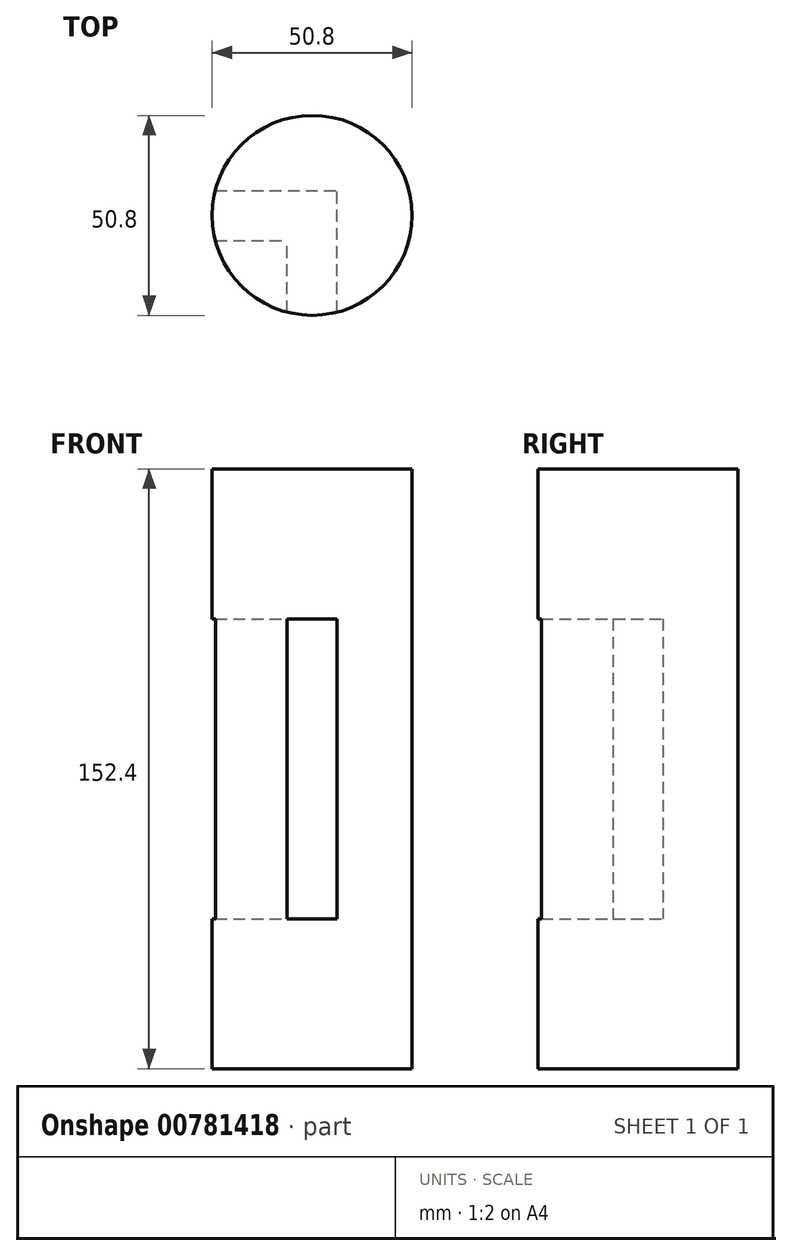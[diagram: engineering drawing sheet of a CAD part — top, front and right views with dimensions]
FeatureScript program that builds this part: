
annotation { "Feature Type Name" : "Feature", "Feature Type Description" : "" }
export const myFeature = defineFeature(function(context is Context, id is Id, definition is map)
    precondition{}
    {
        {
            var Q0;
            Q0=qCreatedBy(makeId("Top.planeOp"),FACE);
            var sketch = newSketch(context, id + "F0", { "sketchPlane" : qUnion([Q0])});
            skCircle(sketch, "E0", {"center": v(0, 0) * mm, "radius": 25.4 * mm});
            skSolve(sketch);
        }
        {
            var Q0;
            Q0=makeQuery(id+"F0.imprint","IMPRINT",FACE,{"disambiguationData":[TD([[makeQuery(id+"F0.imprint","IMPRINT",EDGE,{"derivedFrom":sQuery(id+"F0.wireOp",EDGE,"E0")}),1.0]])]});
            extrude(context, id + "F1", {"entities" : qUnion([Q0]), "depth" : 152.4 * mm, "offsetDistance" : 25.4 * mm});
        }
        {
            var Q0;
            Q0=qCreatedBy(makeId("Right.planeOp"),FACE);
            var sketch = newSketch(context, id + "F2", { "sketchPlane" : qUnion([Q0])});
            skLineSegment(sketch, "E1.bottom", {"start": v(-6.35, 38.1) * mm, "end": v(6.35, 38.1) * mm});
            skLineSegment(sketch, "E1.top", {"start": v(-6.35, 114.3) * mm, "end": v(6.35, 114.3) * mm});
            skLineSegment(sketch, "E1.left", {"start": v(-6.35, 38.1) * mm, "end": v(-6.35, 114.3) * mm});
            skLineSegment(sketch, "E1.right", {"start": v(6.35, 38.1) * mm, "end": v(6.35, 114.3) * mm});
            skPoint(sketch, "E1.middle", {"position": v(0, 76.2) * mm});
            skSolve(sketch);
        }
        {
            var Q0;
            Q0 = qSketchRegion(id + "F2", true);
            extrude(context, id + "F3", {"entities" : qUnion([Q0]), "operationType" : NewBodyOperationType.REMOVE, "oppositeDirection" : true, "depth" : 25.4 * mm, "offsetDistance" : 25.4 * mm});
        }
        {
            var Q0;
            Q0=qCreatedBy(makeId("Front.planeOp"),FACE);
            var sketch = newSketch(context, id + "F4", { "sketchPlane" : qUnion([Q0])});
            skLineSegment(sketch, "E2.bottom", {"start": v(6.35, 114.3) * mm, "end": v(-6.35, 114.3) * mm});
            skLineSegment(sketch, "E2.top", {"start": v(6.35, 38.1) * mm, "end": v(-6.35, 38.1) * mm});
            skLineSegment(sketch, "E2.left", {"start": v(6.35, 114.3) * mm, "end": v(6.35, 38.1) * mm});
            skLineSegment(sketch, "E2.right", {"start": v(-6.35, 114.3) * mm, "end": v(-6.35, 38.1) * mm});
            skPoint(sketch, "E2.middle", {"position": v(0, 76.2) * mm});
            skSolve(sketch);
        }
        {
            var Q0;
            Q0 = qSketchRegion(id + "F4", true);
            extrude(context, id + "F5", {"entities" : qUnion([Q0]), "operationType" : NewBodyOperationType.REMOVE, "depth" : 38.1 * mm, "offsetDistance" : 25.4 * mm});
        }
        {
            var Q0;
            Q0=makeQuery(id+"F5.boolean.opBoolean","COPY",FACE,{"derivedFrom":makeQuery(id+"F5.opExtrude","CAP_FACE",FACE,{"disambiguationData":[OSD([sQuery(id+"F4.wireOp",EDGE,"E2.bottom"),sQuery(id+"F4.wireOp",EDGE,"E2.top"),sQuery(id+"F4.wireOp",EDGE,"E2.left"),sQuery(id+"F4.wireOp",EDGE,"E2.right")])],"isStart":true})});
            extrude(context, id + "F6", {"entities" : qUnion([Q0]), "operationType" : NewBodyOperationType.REMOVE, "oppositeDirection" : true, "depth" : 6.35 * mm, "offsetDistance" : 25.4 * mm});
        }
    });
